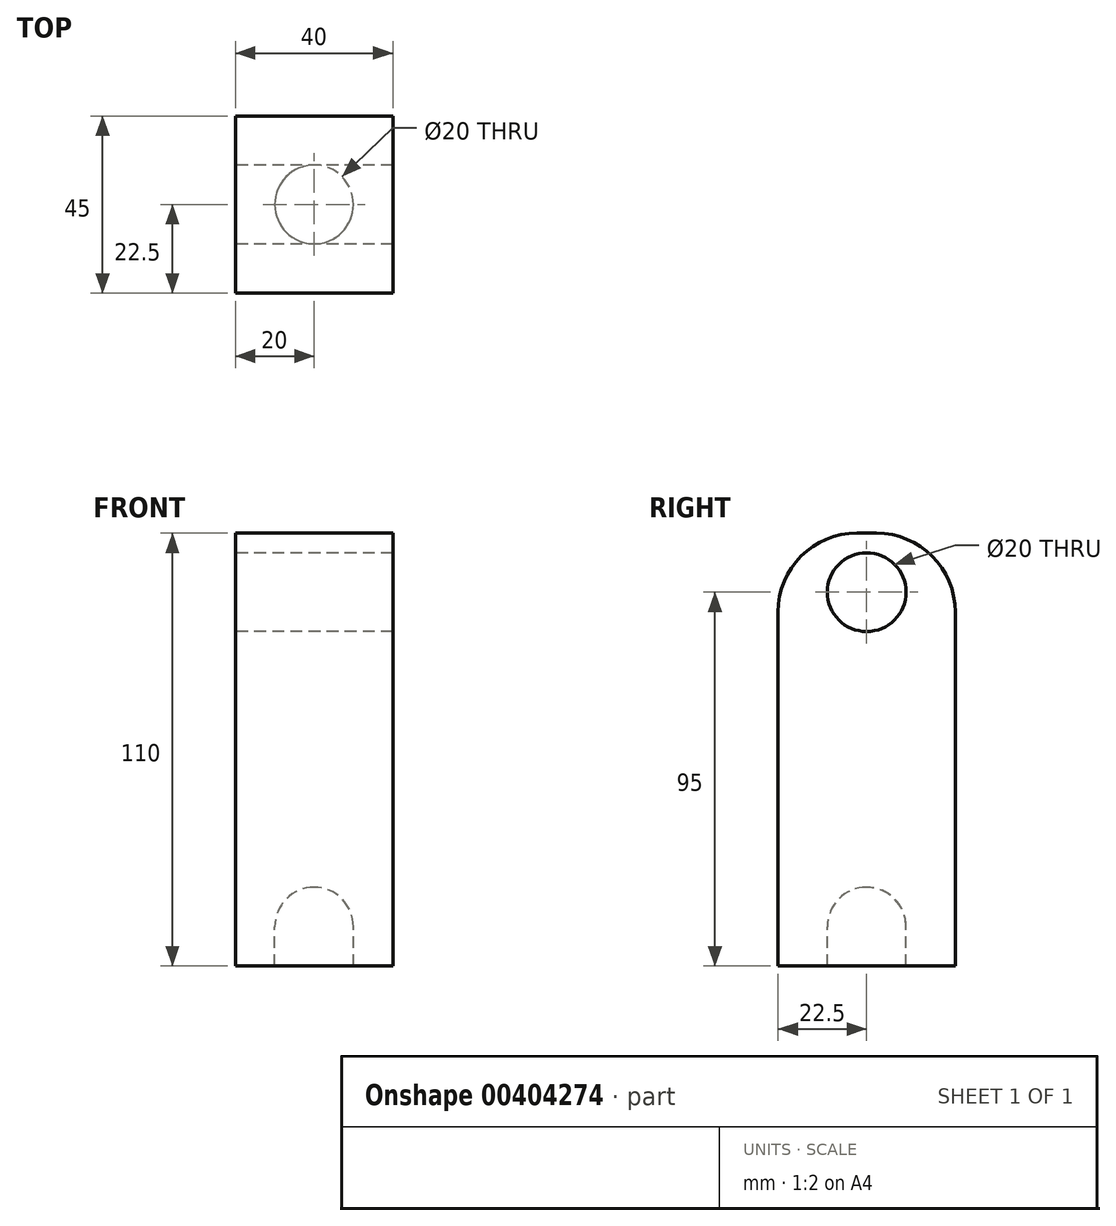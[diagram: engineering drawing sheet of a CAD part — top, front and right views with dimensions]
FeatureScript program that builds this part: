
annotation { "Feature Type Name" : "Feature", "Feature Type Description" : "" }
export const myFeature = defineFeature(function(context is Context, id is Id, definition is map)
    precondition{}
    {
        {
            var Q0;
            Q0=qCreatedBy(makeId("Right.planeOp"),FACE);
            var sketch = newSketch(context, id + "F0", { "sketchPlane" : qUnion([Q0])});
            skLineSegment(sketch, "E0.bottom", {"start": v(22.5, 0) * mm, "end": v(-22.5, 0) * mm});
            skLineSegment(sketch, "E0.top", {"start": v(22.5, 110) * mm, "end": v(-22.5, 110) * mm});
            skLineSegment(sketch, "E0.left", {"start": v(22.5, 0) * mm, "end": v(22.5, 110) * mm});
            skLineSegment(sketch, "E0.right", {"start": v(-22.5, 0) * mm, "end": v(-22.5, 110) * mm});
            skPoint(sketch, "E0.middle", {"position": v(0, 55) * mm});
            skLineSegment(sketch, "E1", {"start": v(0, 110) * mm, "end": v(0, 0) * mm});
            skCircle(sketch, "E2", {"center": v(0, 95) * mm, "radius": 10 * mm});
            skSolve(sketch);
        }
        {
            var Q0;
            {var subQ0=sQuery(id+"F0.wireOp",EDGE,"E0.right");Q0=makeQuery(id+"F0.imprint","IMPRINT",FACE,{"disambiguationData":[TD([[makeQuery(id+"F0.imprint","IMPRINT",EDGE,{"derivedFrom":subQ0}),-1.0]])]});}
            var Q1;
            {var subQ5=sQuery(id+"F0.wireOp",EDGE,"E0.left");Q1=makeQuery(id+"F0.imprint","IMPRINT",FACE,{"disambiguationData":[TD([[makeQuery(id+"F0.imprint","IMPRINT",EDGE,{"derivedFrom":subQ5}),1.0]])]});}
            extrude(context, id + "F1", {"entities" : qUnion([Q0, Q1]), "endBound" : BoundingType.SYMMETRIC, "depth" : 40 * mm});
        }
        {
            var Q0;
            Q0=makeQuery(id+"F1.opExtrude","SWEPT_EDGE",EDGE,{"disambiguationData":[OSD([sQuery(id+"F0.wireOp",EDGE,"E0.top"),sQuery(id+"F0.wireOp",EDGE,"E0.right")])]});
            var Q1;
            Q1=makeQuery(id+"F1.opExtrude","SWEPT_EDGE",EDGE,{"disambiguationData":[OSD([sQuery(id+"F0.wireOp",EDGE,"E0.top"),sQuery(id+"F0.wireOp",EDGE,"E0.left")])]});
            fillet(context, id + "F2", {"entities" : qUnion([Q0, Q1]), "radius" : 20 * mm, "tangentPropagation" : true, "allowEdgeOverflow" : false});
        }
        {
            var Q0;
            Q0=qCreatedBy(makeId("Right.planeOp"),FACE);
            var sketch = newSketch(context, id + "F3", { "sketchPlane" : qUnion([Q0])});
            skLineSegment(sketch, "E3", {"start": v(0, 0) * mm, "end": v(0, 20) * mm});
            skLineSegment(sketch, "E4", {"start": v(10, 10) * mm, "end": v(10, 0) * mm});
            skLineSegment(sketch, "E5.top", {"start": v(0, -5) * mm, "end": v(10, -5) * mm});
            skLineSegment(sketch, "E5.left", {"start": v(0, 0) * mm, "end": v(0, -5) * mm});
            skLineSegment(sketch, "E5.right", {"start": v(10, 0) * mm, "end": v(10, -5) * mm});
            skArc(sketch, "E6", {"start": v(10, 10) * mm, "mid": v(7.07, 17.07) * mm, "end": v(0, 20) * mm});
            skSolve(sketch);
        }
        {
            var Q0;
            Q0=makeQuery(id+"F3.imprint","IMPRINT",FACE,{"disambiguationData":[TD([[makeQuery(id+"F3.imprint","IMPRINT",EDGE,{"derivedFrom":sQuery(id+"F3.wireOp",EDGE,"E3")}),-1.0]])]});
            var Q1;
            Q1=sQuery(id+"F3.wireOp",EDGE,"E3");
            revolve(context, id + "F4", {"operationType" : NewBodyOperationType.REMOVE, "entities" : qUnion([Q0]), "axis" : qUnion([Q1]), "revolveType" : RevolveType.FULL, "oppositeDirection" : true});
        }
    });
